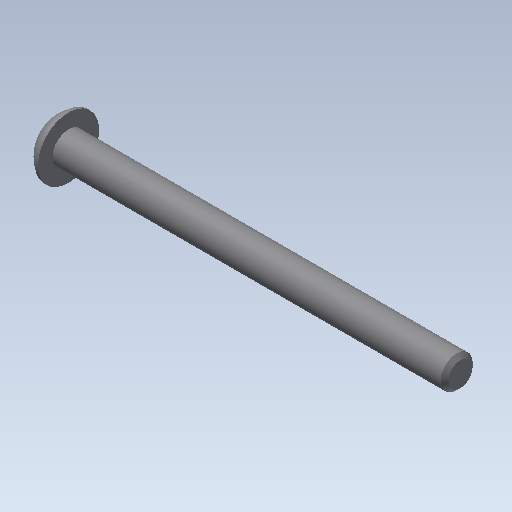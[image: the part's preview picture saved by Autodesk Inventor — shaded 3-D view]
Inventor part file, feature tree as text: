
AUTODESK INVENTOR PART (.ipt)
format: ipt  version: 2020 (Build 240168000, 168)  size: 125,952 bytes
history: native  units: in
note: dims shown in document units (in); Inventor stores cm internally (conversion verified against a paired STEP export)
features: other x3, extrude x1, chamfer x1, imported_body x1, sketch x1
ambient origin geometry x8: Origin, YZ Plane, XZ Plane, XY Plane, X Axis, Y Axis, Z Axis, Center Point
bodies: Body1 (feature_tree)
feature tree (7):
  other  "Bolt 2.0 inch"
  parser-record x1  (decoder bookkeeping rows leaked as tree rows — omitted from the tree; the rows remain in map.json)
  other  "Bolt"
  extrude  "thread length"  Depth=2.0in TaperAngle=0.0deg
  chamfer  "thread chamfer"  Distance=0.02in Angle=45.0deg
  imported_body  "Base1"
  sketch  "Sketch1"  dims[d0=0.164in d1=2.0in d2=0.0in d3=0.02in d4=0.125in d5=45.0deg d7=0.0in d9=0.0in]
